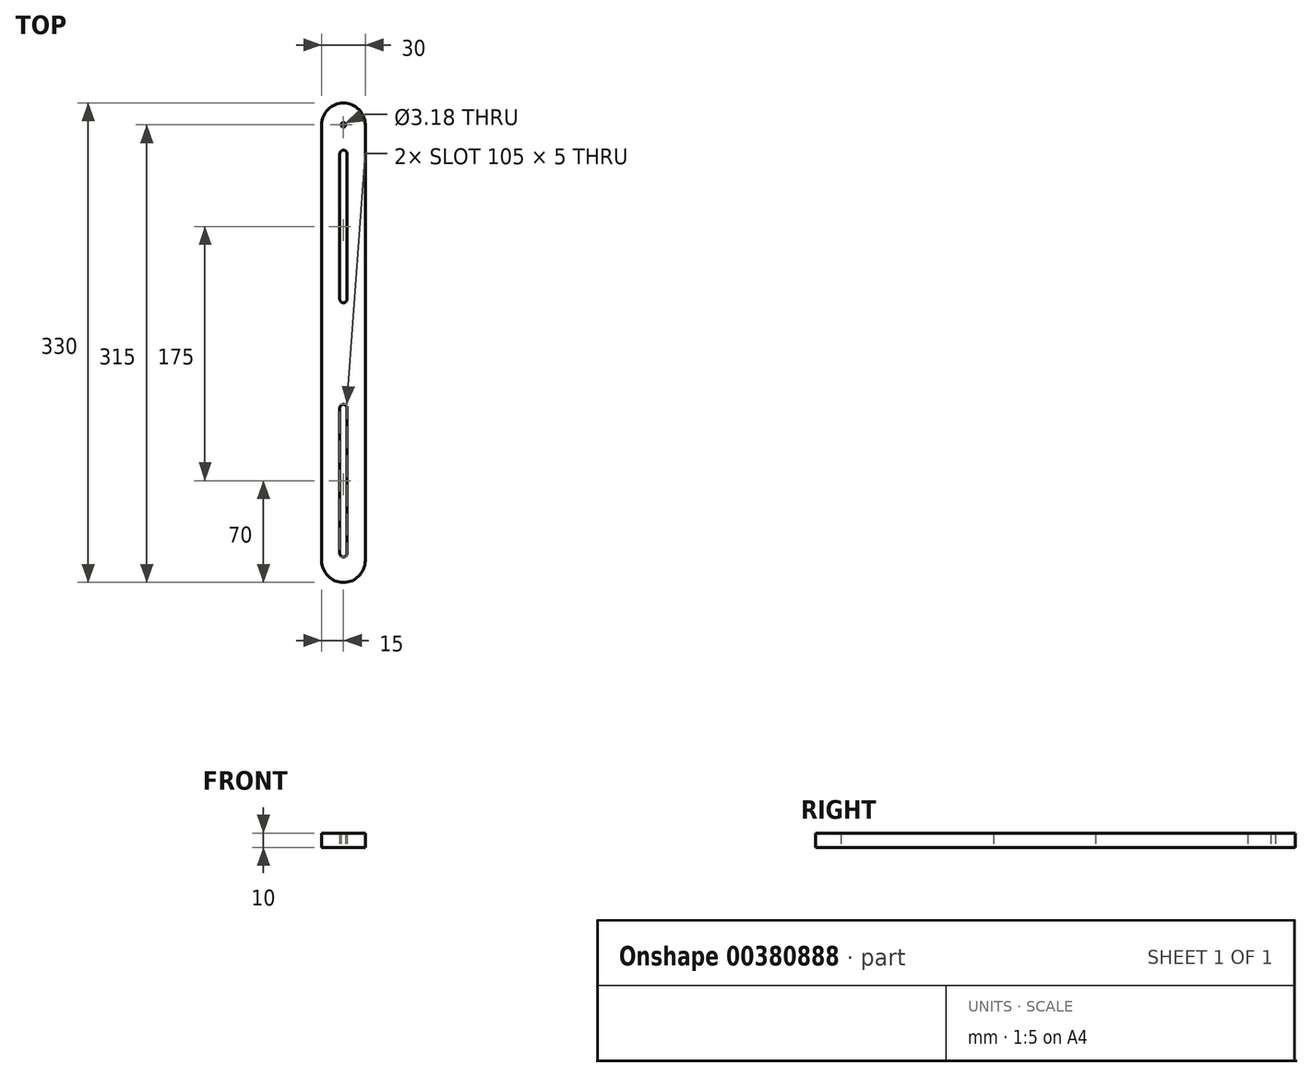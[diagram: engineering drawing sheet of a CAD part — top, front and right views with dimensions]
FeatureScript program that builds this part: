
annotation { "Feature Type Name" : "Feature", "Feature Type Description" : "" }
export const myFeature = defineFeature(function(context is Context, id is Id, definition is map)
    precondition{}
    {
        {
            var Q0;
            Q0=qCreatedBy(makeId("Top.planeOp"),FACE);
            var sketch = newSketch(context, id + "F0", { "sketchPlane" : qUnion([Q0])});
            skLineSegment(sketch, "E0", {"start": v(0, 0) * mm, "end": v(0, -300) * mm});
            skArc(sketch, "E1.0.startCap", {"start": v(-15, 0) * mm, "mid": v(0, 15) * mm, "end": v(15, 0) * mm});
            skArc(sketch, "E1.0.endCap", {"start": v(15, -300) * mm, "mid": v(0, -315) * mm, "end": v(-15, -300) * mm});
            skLineSegment(sketch, "E1.0.left", {"start": v(15, 0) * mm, "end": v(15, -300) * mm});
            skLineSegment(sketch, "E1.0.right", {"start": v(-15, 0) * mm, "end": v(-15, -300) * mm});
            skLineSegment(sketch, "E2", {"start": v(0, -20) * mm, "end": v(0, -120) * mm});
            skArc(sketch, "E3.0.startCap", {"start": v(-2.5, -20) * mm, "mid": v(0, -17.5) * mm, "end": v(2.5, -20) * mm});
            skArc(sketch, "E3.0.endCap", {"start": v(2.5, -120) * mm, "mid": v(0, -122.5) * mm, "end": v(-2.5, -120) * mm});
            skLineSegment(sketch, "E3.0.left", {"start": v(2.5, -20) * mm, "end": v(2.5, -120) * mm});
            skLineSegment(sketch, "E3.0.right", {"start": v(-2.5, -20) * mm, "end": v(-2.5, -120) * mm});
            skCircle(sketch, "E4", {"center": v(0, 0) * mm, "radius": 1.6 * mm});
            skLineSegment(sketch, "E5", {"start": v(0, -195) * mm, "end": v(0, -295) * mm});
            skArc(sketch, "E6.0.startCap", {"start": v(-2.5, -195) * mm, "mid": v(0, -192.5) * mm, "end": v(2.5, -195) * mm});
            skArc(sketch, "E6.0.endCap", {"start": v(2.5, -295) * mm, "mid": v(0, -297.5) * mm, "end": v(-2.5, -295) * mm});
            skLineSegment(sketch, "E6.0.left", {"start": v(2.5, -195) * mm, "end": v(2.5, -295) * mm});
            skLineSegment(sketch, "E6.0.right", {"start": v(-2.5, -195) * mm, "end": v(-2.5, -295) * mm});
            skSolve(sketch);
        }
        {
            var Q0;
            Q0=qSketchRegion(id+"F0",true);
            extrude(context, id + "F1", {"entities" : qUnion([Q0]), "depth" : 10 * mm});
        }
    });
